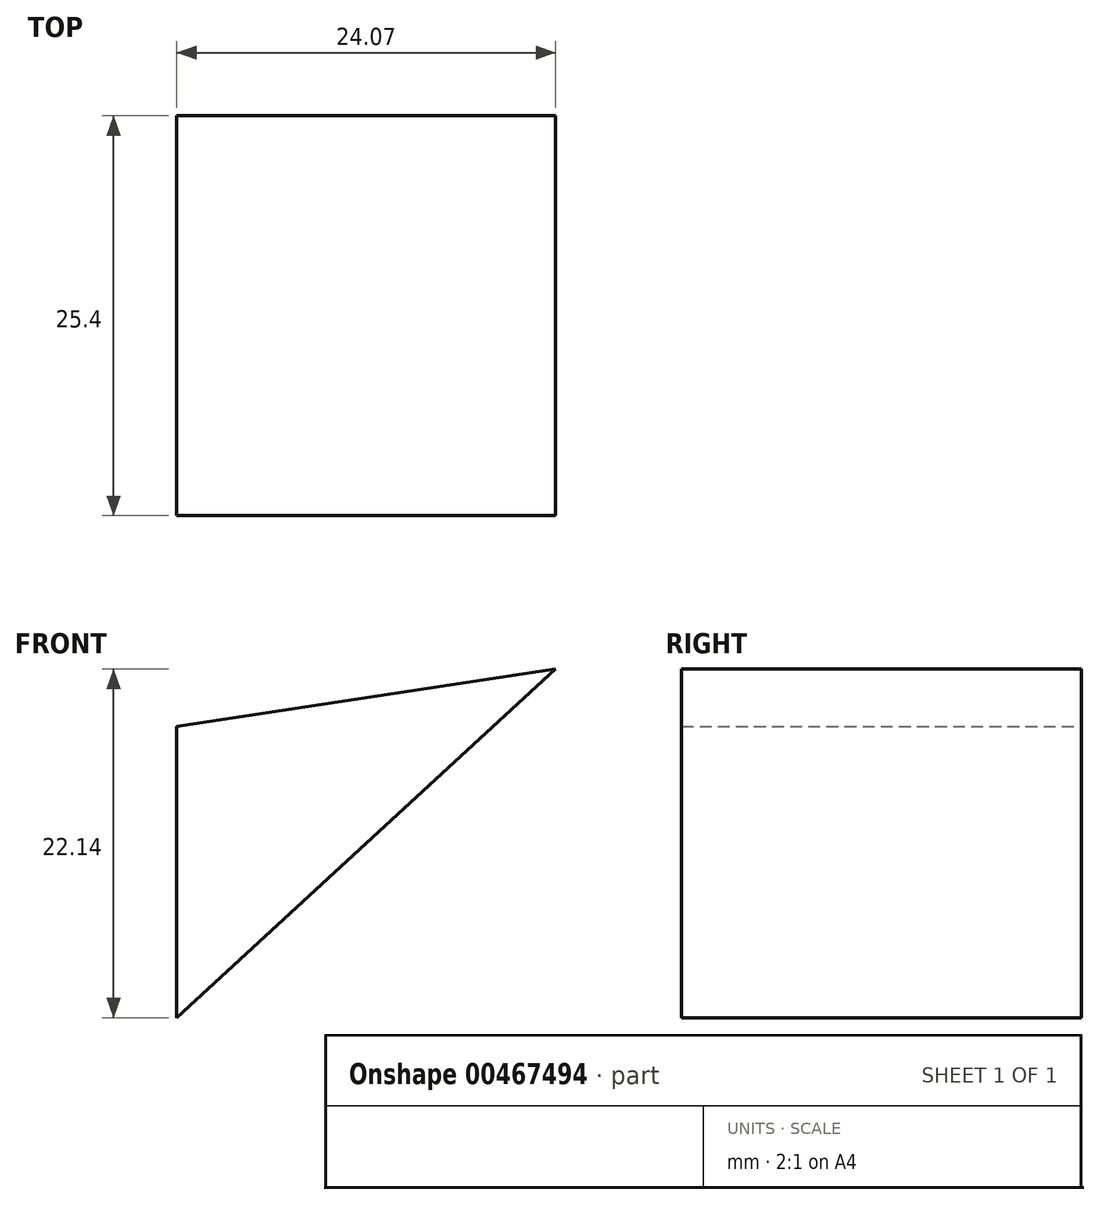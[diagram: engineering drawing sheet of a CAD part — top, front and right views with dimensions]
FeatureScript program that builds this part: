
annotation { "Feature Type Name" : "Feature", "Feature Type Description" : "" }
export const myFeature = defineFeature(function(context is Context, id is Id, definition is map)
    precondition{}
    {
        {
            var Q0;
            Q0=qCreatedBy(makeId("Front.planeOp"),FACE);
            var sketch = newSketch(context, id + "F0", { "sketchPlane" : qUnion([Q0])});
            skLineSegment(sketch, "E0", {"start": v(-86.72, 18.5) * mm, "end": v(-86.72, 0) * mm});
            skLineSegment(sketch, "E1", {"start": v(-86.72, 0) * mm, "end": v(-62.65, 22.14) * mm});
            skLineSegment(sketch, "E2", {"start": v(-62.65, 22.14) * mm, "end": v(-86.72, 18.5) * mm});
            skSolve(sketch);
        }
        {
            var Q0;
            Q0=makeQuery(id+"F0.imprint","IMPRINT",FACE,{"disambiguationData":[TD([[makeQuery(id+"F0.imprint","IMPRINT",EDGE,{"derivedFrom":sQuery(id+"F0.wireOp",EDGE,"E0")}),1.0]])]});
            extrude(context, id + "F1", {"entities" : qUnion([Q0]), "depth" : 25.4 * mm});
        }
    });
